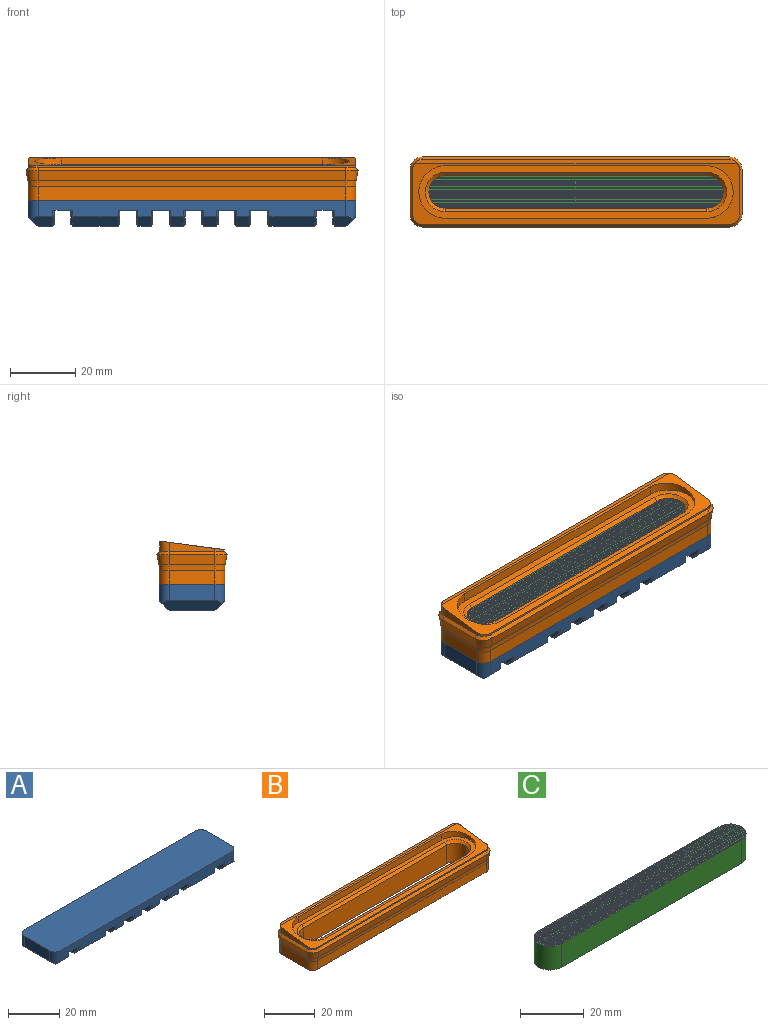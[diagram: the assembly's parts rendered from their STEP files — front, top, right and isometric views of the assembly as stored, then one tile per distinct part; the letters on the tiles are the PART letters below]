
ASSEMBLY  parts=3 mates=2
PART A: 123 faces, bbox 100x20x8 mm
  f0: plane 14x4.5mm, normal (0,0,-1), area 63mm2, adj f28,f29,f30,f120
  f1: plane 14x14mm, normal (0,0,-1), area 196mm2, adj f9,f16,f110,f115
  f2: plane 14x4mm, normal (0,0,-1), area 56mm2, adj f10,f17,f100,f105
  f3: plane 14x4mm, normal (0,0,-1), area 56mm2, adj f11,f18,f90,f95
  f4: plane 14x4mm, normal (0,0,-1), area 56mm2, adj f12,f19,f82,f86
  f5: plane 14x4mm, normal (0,0,-1), area 56mm2, adj f13,f20,f73,f77
  f6: plane 14x14mm, normal (0,0,-1), area 196mm2, adj f14,f21,f63,f69
  f7: plane 94x5mm, normal (0,1,0), area 388.5mm2, adj f9,f10,f11,f12,f13,f14,f15,f25
  f8: plane 94x5mm, normal (0,-1,0), area 386mm2, adj f16,f17,f18,f19,f20,f21,f22,f25
  f9: plane 14x3mm, normal (0,0.71,-0.71), area 59.4mm2, adj f1,f7,f109,f116
  f10: plane 4x3mm, normal (0,0.71,-0.71), area 17mm2, adj f2,f7,f99,f106
  f11: plane 4x3mm, normal (0,0.71,-0.71), area 17mm2, adj f3,f7,f89,f94
  f12: plane 4x3mm, normal (0,0.71,-0.71), area 17mm2, adj f4,f7,f83,f87
  f13: plane 4x3mm, normal (0,0.71,-0.71), area 17mm2, adj f5,f7,f74,f76
  f14: plane 14x3mm, normal (0,0.71,-0.71), area 59.4mm2, adj f6,f7,f62,f67
  f15: plane 5.62x3mm, normal (0,0.71,-0.71), area 19.8mm2, adj f7,f26,f27,f31,f57
  f16: plane 14x3mm, normal (0,-0.71,-0.71), area 59.4mm2, adj f1,f8,f111,f114
  f17: plane 4x3mm, normal (0,-0.71,-0.71), area 17mm2, adj f2,f8,f101,f104
  f18: plane 4x3mm, normal (0,-0.71,-0.71), area 17mm2, adj f3,f8,f91,f96
  f19: plane 4x3mm, normal (0,-0.71,-0.71), area 17mm2, adj f4,f8,f81,f85
  f20: plane 4x3mm, normal (0,-0.71,-0.71), area 17mm2, adj f5,f8,f72,f78
  f21: plane 14x3mm, normal (0,-0.71,-0.71), area 59.4mm2, adj f6,f8,f64,f70
  f22: plane 5.62x3mm, normal (0,-0.71,-0.71), area 19.8mm2, adj f8,f26,f27,f34,f59
  f23: plane 14x5mm, normal (1,0,0), area 70mm2, adj f25,f27,f31,f34
  f24: plane 14x5mm, normal (-1,0,0), area 70mm2, adj f25,f30,f32,f33
  f25: plane 100x20mm, normal (0,0,1), area 1992.3mm2, adj f7,f8,f23,f24,f31,f32,f33,f34
  f26: plane 14x3.5mm, normal (0,0,-1), area 49mm2, adj f15,f22,f27,f58
  f27: plane 18.24x3mm, normal (0.71,0,-0.71), area 69.4mm2, adj f15,f22,f23,f26,f31,f34
  f28: plane 6.62x3mm, normal (0,0.71,-0.71), area 24.1mm2, adj f0,f7,f30,f32,f121
  f29: plane 6.62x3mm, normal (0,-0.71,-0.71), area 24.1mm2, adj f0,f8,f30,f33,f119
  f30: plane 18.24x3mm, normal (-0.71,0,-0.71), area 69.4mm2, adj f0,f24,f28,f29,f32,f33
  f31: cylinder r=3mm len=5.88mm, axis (0,0,1), area 25mm2, adj f7,f15,f23,f25,f27
  f32: cylinder r=3mm len=5.88mm, axis (0,0,-1), area 25mm2, adj f7,f24,f25,f28,f30
  f33: cylinder r=3mm len=5.88mm, axis (0,0,1), area 25mm2, adj f8,f24,f25,f29,f30
  f34: cylinder r=3mm len=5.88mm, axis (0,0,-1), area 25mm2, adj f8,f22,f23,f25,f27
  f35: plane 20x6mm, normal (0,0,-1), area 100.5mm2, adj f7,f8,f36,f37,f56,f60,f61,f65
  f36: plane 19x4.5mm, normal (-1,0,0), area 78.2mm2, adj f35,f56,f57,f58,f59,f60
  f37: plane 19x4.5mm, normal (1,0,0), area 78.2mm2, adj f35,f61,f62,f63,f64,f65
  f38: plane 20x6mm, normal (0,0,-1), area 100.5mm2, adj f7,f8,f39,f40,f66,f68,f71,f75
  f39: plane 19x4.5mm, normal (-1,0,0), area 78.2mm2, adj f38,f66,f67,f68,f69,f70
  f40: plane 19x4.5mm, normal (1,0,0), area 78.2mm2, adj f38,f71,f72,f73,f74,f75
  f41: plane 20x6mm, normal (0,0,-1), area 100.2mm2, adj f7,f8,f42,f43,f79,f80
  f42: plane 19.5x4.5mm, normal (-1,0,0), area 78.9mm2, adj f7,f41,f76,f77,f78,f79
  f43: plane 19.5x4.5mm, normal (1,0,0), area 78.9mm2, adj f7,f41,f80,f81,f82,f83
  f44: plane 20x6mm, normal (0,0,-1), area 100.4mm2, adj f7,f8,f45,f46,f84,f88,f92
  f45: plane 19.5x4.5mm, normal (-1,0,0), area 78.9mm2, adj f7,f44,f84,f85,f86,f87
  f46: plane 19x4.5mm, normal (1,0,0), area 78.2mm2, adj f44,f88,f89,f90,f91,f92
  f47: plane 20x6mm, normal (0,0,-1), area 100.5mm2, adj f7,f8,f48,f49,f93,f97,f98,f102
  f48: plane 19x4.5mm, normal (-1,0,0), area 78.2mm2, adj f47,f93,f94,f95,f96,f97
  f49: plane 19x4.5mm, normal (1,0,0), area 78.2mm2, adj f47,f98,f99,f100,f101,f102
  f50: plane 20x6mm, normal (0,0,-1), area 100.5mm2, adj f7,f8,f51,f52,f103,f107,f108,f112
  f51: plane 19x4.5mm, normal (-1,0,0), area 78.2mm2, adj f50,f103,f104,f105,f106,f107
  f52: plane 19x4.5mm, normal (1,0,0), area 78.2mm2, adj f50,f108,f109,f110,f111,f112
  f53: plane 20x6mm, normal (0,0,-1), area 100.5mm2, adj f7,f8,f54,f55,f113,f117,f118,f122
  f54: plane 19x4.5mm, normal (-1,0,0), area 78.2mm2, adj f53,f113,f114,f115,f116,f117
  f55: plane 19x4.5mm, normal (1,0,0), area 78.2mm2, adj f53,f118,f119,f120,f121,f122
  f56: plane 2x0.5mm, normal (-0.71,0.71,0), area 1.3mm2, adj f7,f35,f36,f57
  f57: plane 3.21x3.21mm, normal (-0.71,0.5,-0.5), area 2.9mm2, adj f15,f36,f56,f58
  f58: plane 14x0.5mm, normal (-0.71,0,-0.71), area 9.8mm2, adj f26,f36,f57,f59
  f59: plane 3.21x3.21mm, normal (-0.71,-0.5,-0.5), area 2.9mm2, adj f22,f36,f58,f60
  f60: plane 2x0.5mm, normal (-0.71,-0.71,0), area 1.3mm2, adj f8,f35,f36,f59
  f61: plane 2x0.5mm, normal (0.71,0.71,0), area 1.3mm2, adj f7,f35,f37,f62
  f62: plane 3.21x3.21mm, normal (0.71,0.5,-0.5), area 2.9mm2, adj f14,f37,f61,f63
  f63: plane 14x0.5mm, normal (0.71,0,-0.71), area 9.8mm2, adj f6,f37,f62,f64
  f64: plane 3.21x3.21mm, normal (0.71,-0.5,-0.5), area 2.9mm2, adj f21,f37,f63,f65
  f65: plane 2x0.5mm, normal (0.71,-0.71,0), area 1.3mm2, adj f8,f35,f37,f64
  f66: plane 2x0.5mm, normal (-0.71,0.71,0), area 1.3mm2, adj f7,f38,f39,f67
  f67: plane 3.21x3.21mm, normal (-0.71,0.5,-0.5), area 2.9mm2, adj f14,f39,f66,f69
  f68: plane 2x0.5mm, normal (-0.71,-0.71,0), area 1.3mm2, adj f8,f38,f39,f70
  f69: plane 14x0.5mm, normal (-0.71,0,-0.71), area 9.8mm2, adj f6,f39,f67,f70
  f70: plane 3.21x3.21mm, normal (-0.71,-0.5,-0.5), area 2.9mm2, adj f21,f39,f68,f69
  f71: plane 2x0.5mm, normal (0.71,-0.71,0), area 1.3mm2, adj f8,f38,f40,f72
  f72: plane 3.21x3.21mm, normal (0.71,-0.5,-0.5), area 2.9mm2, adj f20,f40,f71,f73
  f73: plane 14x0.5mm, normal (0.71,0,-0.71), area 9.8mm2, adj f5,f40,f72,f74
  f74: plane 3.21x3.21mm, normal (0.71,0.5,-0.5), area 2.9mm2, adj f13,f40,f73,f75
  f75: plane 2x0.5mm, normal (0.71,0.71,0), area 1.3mm2, adj f7,f38,f40,f74
  f76: plane 3.71x3.21mm, normal (-0.71,0.5,-0.5), area 3.1mm2, adj f7,f13,f42,f77
  f77: plane 14x0.5mm, normal (-0.71,0,-0.71), area 9.8mm2, adj f5,f42,f76,f78
  f78: plane 3.21x3.21mm, normal (-0.71,-0.5,-0.5), area 2.9mm2, adj f20,f42,f77,f79
  f79: plane 2x0.5mm, normal (-0.71,-0.71,0), area 1.3mm2, adj f8,f41,f42,f78
  f80: plane 2x0.5mm, normal (0.71,-0.71,0), area 1.3mm2, adj f8,f41,f43,f81
  f81: plane 3.21x3.21mm, normal (0.71,-0.5,-0.5), area 2.9mm2, adj f19,f43,f80,f82
  f82: plane 14x0.5mm, normal (0.71,0,-0.71), area 9.8mm2, adj f4,f43,f81,f83
  f83: plane 3.71x3.21mm, normal (0.71,0.5,-0.5), area 3.1mm2, adj f7,f12,f43,f82
  f84: plane 2x0.5mm, normal (-0.71,-0.71,0), area 1.3mm2, adj f8,f44,f45,f85
  f85: plane 3.21x3.21mm, normal (-0.71,-0.5,-0.5), area 2.9mm2, adj f19,f45,f84,f86
  f86: plane 14x0.5mm, normal (-0.71,0,-0.71), area 9.8mm2, adj f4,f45,f85,f87
  f87: plane 3.71x3.21mm, normal (-0.71,0.5,-0.5), area 3.1mm2, adj f7,f12,f45,f86
  f88: plane 2x0.5mm, normal (0.71,0.71,0), area 1.3mm2, adj f7,f44,f46,f89
  f89: plane 3.21x3.21mm, normal (0.71,0.5,-0.5), area 2.9mm2, adj f11,f46,f88,f90
  f90: plane 14x0.5mm, normal (0.71,0,-0.71), area 9.8mm2, adj f3,f46,f89,f91
  f91: plane 3.21x3.21mm, normal (0.71,-0.5,-0.5), area 2.9mm2, adj f18,f46,f90,f92
  f92: plane 2x0.5mm, normal (0.71,-0.71,0), area 1.3mm2, adj f8,f44,f46,f91
  f93: plane 2x0.5mm, normal (-0.71,0.71,0), area 1.3mm2, adj f7,f47,f48,f94
  f94: plane 3.21x3.21mm, normal (-0.71,0.5,-0.5), area 2.9mm2, adj f11,f48,f93,f95
  f95: plane 14x0.5mm, normal (-0.71,0,-0.71), area 9.8mm2, adj f3,f48,f94,f96
  f96: plane 3.21x3.21mm, normal (-0.71,-0.5,-0.5), area 2.9mm2, adj f18,f48,f95,f97
  f97: plane 2x0.5mm, normal (-0.71,-0.71,0), area 1.3mm2, adj f8,f47,f48,f96
  f98: plane 2x0.5mm, normal (0.71,0.71,0), area 1.3mm2, adj f7,f47,f49,f99
  f99: plane 3.21x3.21mm, normal (0.71,0.5,-0.5), area 2.9mm2, adj f10,f49,f98,f100
  f100: plane 14x0.5mm, normal (0.71,0,-0.71), area 9.8mm2, adj f2,f49,f99,f101
  f101: plane 3.21x3.21mm, normal (0.71,-0.5,-0.5), area 2.9mm2, adj f17,f49,f100,f102
  f102: plane 2x0.5mm, normal (0.71,-0.71,0), area 1.3mm2, adj f8,f47,f49,f101
  f103: plane 2x0.5mm, normal (-0.71,-0.71,0), area 1.3mm2, adj f8,f50,f51,f104
  f104: plane 3.21x3.21mm, normal (-0.71,-0.5,-0.5), area 2.9mm2, adj f17,f51,f103,f105
  f105: plane 14x0.5mm, normal (-0.71,0,-0.71), area 9.8mm2, adj f2,f51,f104,f106
  f106: plane 3.21x3.21mm, normal (-0.71,0.5,-0.5), area 2.9mm2, adj f10,f51,f105,f107
  f107: plane 2x0.5mm, normal (-0.71,0.71,0), area 1.3mm2, adj f7,f50,f51,f106
  f108: plane 2x0.5mm, normal (0.71,0.71,0), area 1.3mm2, adj f7,f50,f52,f109
  f109: plane 3.21x3.21mm, normal (0.71,0.5,-0.5), area 2.9mm2, adj f9,f52,f108,f110
  f110: plane 14x0.5mm, normal (0.71,0,-0.71), area 9.8mm2, adj f1,f52,f109,f111
  f111: plane 3.21x3.21mm, normal (0.71,-0.5,-0.5), area 2.9mm2, adj f16,f52,f110,f112
  f112: plane 2x0.5mm, normal (0.71,-0.71,0), area 1.3mm2, adj f8,f50,f52,f111
  f113: plane 2x0.5mm, normal (-0.71,-0.71,0), area 1.3mm2, adj f8,f53,f54,f114
  f114: plane 3.21x3.21mm, normal (-0.71,-0.5,-0.5), area 2.9mm2, adj f16,f54,f113,f115
  f115: plane 14x0.5mm, normal (-0.71,0,-0.71), area 9.8mm2, adj f1,f54,f114,f116
  f116: plane 3.21x3.21mm, normal (-0.71,0.5,-0.5), area 2.9mm2, adj f9,f54,f115,f117
  f117: plane 2x0.5mm, normal (-0.71,0.71,0), area 1.3mm2, adj f7,f53,f54,f116
  f118: plane 2x0.5mm, normal (0.71,-0.71,0), area 1.3mm2, adj f8,f53,f55,f119
  f119: plane 3.21x3.21mm, normal (0.71,-0.5,-0.5), area 2.9mm2, adj f29,f55,f118,f120
  f120: plane 14x0.5mm, normal (0.71,0,-0.71), area 9.8mm2, adj f0,f55,f119,f121
  f121: plane 3.21x3.21mm, normal (0.71,0.5,-0.5), area 2.9mm2, adj f28,f55,f120,f122
  f122: plane 2x0.5mm, normal (0.71,0.71,0), area 1.3mm2, adj f7,f53,f55,f121
PART B: 56 faces, bbox 106.8x26.8x16 mm
  f0: plane 96x16mm, normal (0,0,1), area 408mm2, adj f38,f39,f40,f41,f42,f43,f44,f53
  f1: plane 100x20mm, normal (0,0,-1), area 1113.7mm2, adj f2,f3,f4,f5,f6,f7,f8,f9
  f2: plane 14x4.13mm, normal (1,0,0), area 57.8mm2, adj f1,f6,f9,f21
  f3: plane 94x4.13mm, normal (0,1,0), area 387.8mm2, adj f1,f6,f7,f18
  f4: plane 14x4.13mm, normal (-1,0,0), area 57.8mm2, adj f1,f7,f8,f22
  f5: plane 94x4.13mm, normal (0,-1,0), area 387.8mm2, adj f1,f8,f9,f25
  f6: cylinder r=3mm len=4.13mm, axis (0,0,1), area 19.4mm2, adj f1,f2,f3,f19
  f7: cylinder r=3mm len=4.13mm, axis (0,0,-1), area 19.4mm2, adj f1,f3,f4,f20
  f8: cylinder r=3mm len=4.13mm, axis (0,0,1), area 19.4mm2, adj f1,f4,f5,f24
  f9: cylinder r=3mm len=4.13mm, axis (0,0,-1), area 19.4mm2, adj f1,f2,f5,f23
  f10: plane 14x3.15mm, normal (0.98,0,-0.17), area 44.8mm2, adj f11,f17,f21,f26
  f11: cone r=3mm half-angle=10deg, axis (0,0,1), area 17.3mm2, adj f10,f12,f19,f27
  f12: plane 94x3.15mm, normal (0,0.98,-0.17), area 301mm2, adj f11,f13,f18,f29
  f13: cone r=3mm half-angle=10deg, axis (0,0,1), area 17.3mm2, adj f12,f14,f20,f31
  f14: plane 14x3.15mm, normal (-0.98,0,-0.17), area 44.8mm2, adj f13,f15,f22,f33
  f15: cone r=3mm half-angle=10deg, axis (0,0,1), area 17.3mm2, adj f14,f16,f24,f32
  f16: plane 94x3.15mm, normal (0,-0.98,-0.17), area 301mm2, adj f15,f17,f25,f30
  f17: cone r=3mm half-angle=10deg, axis (0,0,1), area 17.3mm2, adj f10,f16,f23,f28
  f18: cylinder r=10mm len=94mm, axis (-1,0,0), area 164.1mm2, adj f3,f12,f19,f20
  f19: torus R=13mm, axis (0,0,1), area 8.4mm2, adj f6,f11,f18,f21
  f20: torus R=13mm, axis (0,0,1), area 8.4mm2, adj f7,f13,f18,f22
  f21: cylinder r=10mm len=14mm, axis (0,1,0), area 24.4mm2, adj f2,f10,f19,f23
  f22: cylinder r=10mm len=14mm, axis (0,-1,0), area 24.4mm2, adj f4,f14,f20,f24
  f23: torus R=13mm, axis (0,0,1), area 8.4mm2, adj f9,f17,f21,f25
  f24: torus R=13mm, axis (0,0,1), area 8.4mm2, adj f8,f15,f22,f25
  f25: cylinder r=10mm len=94mm, axis (1,0,0), area 164.1mm2, adj f5,f16,f23,f24
  f26: plane 14x0.99mm, normal (0.77,0,0.64), area 18mm2, adj f10,f27,f28,f50
  f27: cone r=2.88mm half-angle=40deg, axis (0,0,-1), area 6.7mm2, adj f11,f26,f29,f51
  f28: cone r=2.88mm half-angle=40deg, axis (0,0,-1), area 6.7mm2, adj f17,f26,f30,f49
  f29: plane 94x0.99mm, normal (0,0.77,0.64), area 120.8mm2, adj f12,f27,f31,f52
  f30: plane 94x0.99mm, normal (0,-0.77,0.64), area 120.8mm2, adj f16,f28,f32,f48
  f31: cone r=2.88mm half-angle=40deg, axis (0,0,-1), area 6.7mm2, adj f13,f29,f33,f45
  f32: cone r=2.88mm half-angle=40deg, axis (0,0,-1), area 6.7mm2, adj f15,f30,f33,f47
  f33: plane 14x0.99mm, normal (-0.77,0,0.64), area 18mm2, adj f14,f31,f32,f46
  f34: plane 80x9mm, normal (0,-1,0), area 720mm2, adj f1,f36,f37,f38
  f35: plane 80x9mm, normal (0,1,0), area 720mm2, adj f1,f36,f37,f41
  f36: cylinder r=5mm len=10mm, axis (0,0,-1), area 141.4mm2, adj f1,f34,f35,f39
  f37: cylinder r=5mm len=10mm, axis (0,0,1), area 141.4mm2, adj f1,f34,f35,f40
  f38: plane 80x1mm, normal (0,-0.71,0.71), area 113.1mm2, adj f0,f34,f39,f40
  f39: cone r=6mm half-angle=45deg, axis (0,0,1), area 24.4mm2, adj f0,f36,f38,f41
  f40: cone r=6mm half-angle=45deg, axis (0,0,1), area 24.4mm2, adj f0,f37,f38,f41
  f41: plane 80x1mm, normal (0,0.71,0.71), area 113.1mm2, adj f0,f35,f39,f40
  f42: plane 80x2.9mm, normal (0,-1,0), area 232.3mm2, adj f0,f43,f53,f55
  f43: cylinder r=8mm len=16mm, axis (0,0,-1), area 46.4mm2, adj f0,f42,f44,f55
  f44: plane 80x0.79mm, normal (0,1,0), area 63.1mm2, adj f0,f43,f53,f55
  f45: cylinder r=2.88mm len=3mm, axis (0,0,-1), area 13.4mm2, adj f31,f46,f52,f54,f55
  f46: plane 14x2.77mm, normal (-1,0,0), area 25.8mm2, adj f33,f45,f47,f55
  f47: cylinder r=2.88mm len=2.88mm, axis (0,0,-1), area 3.1mm2, adj f32,f46,f48,f55
  f48: plane 94x0.54mm, normal (0,-1,0), area 50.8mm2, adj f30,f47,f49,f55
  f49: cylinder r=2.88mm len=2.88mm, axis (0,0,-1), area 3.1mm2, adj f28,f48,f50,f55
  f50: plane 14x2.77mm, normal (1,0,0), area 25.8mm2, adj f26,f49,f51,f55
  f51: cylinder r=2.88mm len=3mm, axis (0,0,-1), area 13.4mm2, adj f27,f50,f52,f54,f55
  f52: plane 94x3mm, normal (0,1,0), area 282mm2, adj f29,f45,f51,f54
  f53: cylinder r=8mm len=16mm, axis (0,0,-1), area 46.4mm2, adj f0,f42,f44,f55
  f54: plane 98.61x1.15mm, normal (0,0,1), area 111.8mm2, adj f45,f51,f52,f55
  f55: plane 99.78x18.63mm, normal (0,-0.13,0.99), area 374.9mm2, adj f42,f43,f44,f45,f46,f47,f48,f49
PART C: 65 faces, bbox 90x10x9.2 mm
  f0: plane 87.14x0.5mm, normal (0,0,1), area 43.3mm2, adj f13,f14,f58,f61
  f1: plane 88.66x0.5mm, normal (0,0,1), area 44.2mm2, adj f13,f14,f53,f56
  f2: plane 89.54x0.5mm, normal (0,0,1), area 44.7mm2, adj f13,f14,f48,f51
  f3: plane 89.95x0.5mm, normal (0,0,1), area 44.9mm2, adj f13,f14,f43,f46
  f4: plane 90x0.5mm, normal (0,0,1), area 45mm2, adj f13,f14,f38,f41
  f5: plane 89.8x0.5mm, normal (0,0,1), area 44.8mm2, adj f13,f14,f33,f36
  f6: plane 89.17x0.5mm, normal (0,0,1), area 44.5mm2, adj f13,f14,f28,f31
  f7: plane 88x0.5mm, normal (0,0,1), area 43.8mm2, adj f13,f14,f23,f26
  f8: plane 86x0.5mm, normal (0,0,1), area 42.6mm2, adj f13,f14,f15,f21
  f9: plane 84.36x0.5mm, normal (0,0,1), area 41.5mm2, adj f10,f13,f14,f63
  f10: plane 80x9mm, normal (0,1,0), area 720mm2, adj f9,f12,f13,f14
  f11: plane 80x9mm, normal (0,-1,0), area 720mm2, adj f12,f13,f14,f17
  f12: plane 90x10mm, normal (0,0,-1), area 878.5mm2, adj f10,f11,f13,f14
  f13: cylinder r=5mm len=10mm, axis (0,0,-1), area 141.4mm2, adj f0,f1,f2,f3,f4,f5,f6,f7
  f14: cylinder r=5mm len=10mm, axis (0,0,1), area 141.4mm2, adj f0,f1,f2,f3,f4,f5,f6,f7
  f15: plane 84.38x0.22mm, normal (0,0.87,0.5), area 19.4mm2, adj f8,f16,f18,f19
  f16: cone r=5mm half-angle=30deg, axis (0,0,-1), area 0.4mm2, adj f14,f15,f17,f19
  f17: plane 80x0.2mm, normal (0,-0.87,0.5), area 18.5mm2, adj f11,f16,f18,f19
  f18: cone r=5mm half-angle=30deg, axis (0,0,-1), area 0.4mm2, adj f13,f15,f17,f19
  f19: plane 83.2x0.27mm, normal (0,0,1), area 22.1mm2, adj f15,f16,f17,f18
  f20: cone r=5mm half-angle=30deg, axis (0,0,-1), area 0.1mm2, adj f14,f21,f23,f24
  f21: plane 86x0.2mm, normal (0,-0.87,0.5), area 19.9mm2, adj f8,f20,f22,f24
  f22: cone r=5mm half-angle=30deg, axis (0,0,-1), area 0.1mm2, adj f13,f21,f23,f24
  f23: plane 87.15x0.2mm, normal (0,0.87,0.5), area 20.1mm2, adj f7,f20,f22,f24
  f24: plane 86.57x0.27mm, normal (0,0,1), area 23.2mm2, adj f20,f21,f22,f23
  f25: cone r=5mm half-angle=30deg, axis (0,0,-1), area 0.1mm2, adj f14,f26,f28,f29
  f26: plane 88x0.2mm, normal (0,-0.87,0.5), area 20.3mm2, adj f7,f25,f27,f29
  f27: cone r=5mm half-angle=30deg, axis (0,0,-1), area 0.1mm2, adj f13,f26,f28,f29
  f28: plane 88.66x0.2mm, normal (0,0.87,0.5), area 20.4mm2, adj f6,f25,f27,f29
  f29: plane 88.25x0.27mm, normal (0,0,1), area 23.7mm2, adj f25,f26,f27,f28
  f30: cone r=5mm half-angle=30deg, axis (0,0,-1), area 0.1mm2, adj f14,f31,f33,f34
  f31: plane 89.17x0.2mm, normal (0,-0.87,0.5), area 20.6mm2, adj f6,f30,f32,f34
  f32: cone r=5mm half-angle=30deg, axis (0,0,-1), area 0.1mm2, adj f13,f31,f33,f34
  f33: plane 89.54x0.2mm, normal (0,0.87,0.5), area 20.6mm2, adj f5,f30,f32,f34
  f34: plane 89.22x0.27mm, normal (0,0,1), area 24mm2, adj f30,f31,f32,f33
  f35: cone r=5mm half-angle=30deg, axis (0,0,-1), area 0.1mm2, adj f14,f36,f38,f39
  f36: plane 89.8x0.2mm, normal (0,-0.87,0.5), area 20.7mm2, adj f5,f35,f37,f39
  f37: cone r=5mm half-angle=30deg, axis (0,0,-1), area 0.1mm2, adj f13,f36,f38,f39
  f38: plane 89.95x0.2mm, normal (0,0.87,0.5), area 20.7mm2, adj f4,f35,f37,f39
  f39: plane 89.69x0.27mm, normal (0,0,1), area 24.1mm2, adj f35,f36,f37,f38
  f40: cone r=5mm half-angle=30deg, axis (0,0,-1), area 0.1mm2, adj f14,f41,f43,f44
  f41: plane 90x0.2mm, normal (0,-0.87,0.5), area 20.8mm2, adj f4,f40,f42,f44
  f42: cone r=5mm half-angle=30deg, axis (0,0,-1), area 0.1mm2, adj f13,f41,f43,f44
  f43: plane 89.95x0.2mm, normal (0,0.87,0.5), area 20.7mm2, adj f3,f40,f42,f44
  f44: plane 89.77x0.27mm, normal (0,0,1), area 24.1mm2, adj f40,f41,f42,f43
  f45: cone r=5mm half-angle=30deg, axis (0,0,-1), area 0.1mm2, adj f14,f46,f48,f49
  f46: plane 89.8x0.2mm, normal (0,-0.87,0.5), area 20.7mm2, adj f3,f45,f47,f49
  f47: cone r=5mm half-angle=30deg, axis (0,0,-1), area 0.1mm2, adj f13,f46,f48,f49
  f48: plane 89.54x0.2mm, normal (0,0.87,0.5), area 20.7mm2, adj f2,f45,f47,f49
  f49: plane 89.51x0.27mm, normal (0,0,1), area 24.1mm2, adj f45,f46,f47,f48
  f50: cone r=5mm half-angle=30deg, axis (0,0,-1), area 0.1mm2, adj f14,f51,f53,f54
  f51: plane 89.17x0.2mm, normal (0,-0.87,0.5), area 20.6mm2, adj f2,f50,f52,f54
  f52: cone r=5mm half-angle=30deg, axis (0,0,-1), area 0.1mm2, adj f13,f51,f53,f54
  f53: plane 88.66x0.2mm, normal (0,0.87,0.5), area 20.5mm2, adj f1,f50,f52,f54
  f54: plane 88.81x0.27mm, normal (0,0,1), area 23.9mm2, adj f50,f51,f52,f53
  f55: cone r=5mm half-angle=30deg, axis (0,0,-1), area 0.1mm2, adj f14,f56,f58,f59
  f56: plane 88x0.2mm, normal (0,-0.87,0.5), area 20.3mm2, adj f1,f55,f57,f59
  f57: cone r=5mm half-angle=30deg, axis (0,0,-1), area 0.1mm2, adj f13,f56,f58,f59
  f58: plane 87.14x0.2mm, normal (0,0.87,0.5), area 20.1mm2, adj f0,f55,f57,f59
  f59: plane 87.52x0.27mm, normal (0,0,1), area 23.5mm2, adj f55,f56,f57,f58
  f60: cone r=5mm half-angle=30deg, axis (0,0,-1), area 0.2mm2, adj f14,f61,f63,f64
  f61: plane 86.01x0.21mm, normal (0,-0.87,0.5), area 19.8mm2, adj f0,f60,f62,f64
  f62: cone r=5mm half-angle=30deg, axis (0,0,-1), area 0.2mm2, adj f13,f61,f63,f64
  f63: plane 84.36x0.2mm, normal (0,0.87,0.5), area 19.5mm2, adj f9,f60,f62,f64
  f64: plane 85.26x0.27mm, normal (0,0,1), area 22.8mm2, adj f60,f61,f62,f63
PLACE A t=(-6.99,-1.04,0.48)mm
PLACE B t=(-6.99,-1.04,8.48)mm
PLACE C t=(-6.99,-1.04,8.48)mm
MATE fastened B.f1 <-> A.f25  axis (0,0,-1) through (-6.99,-1.04,8.48)mm
MATE fastened C.f12 <-> A.f25  axis (0,0,-1) through (-6.99,-1.04,8.48)mm
